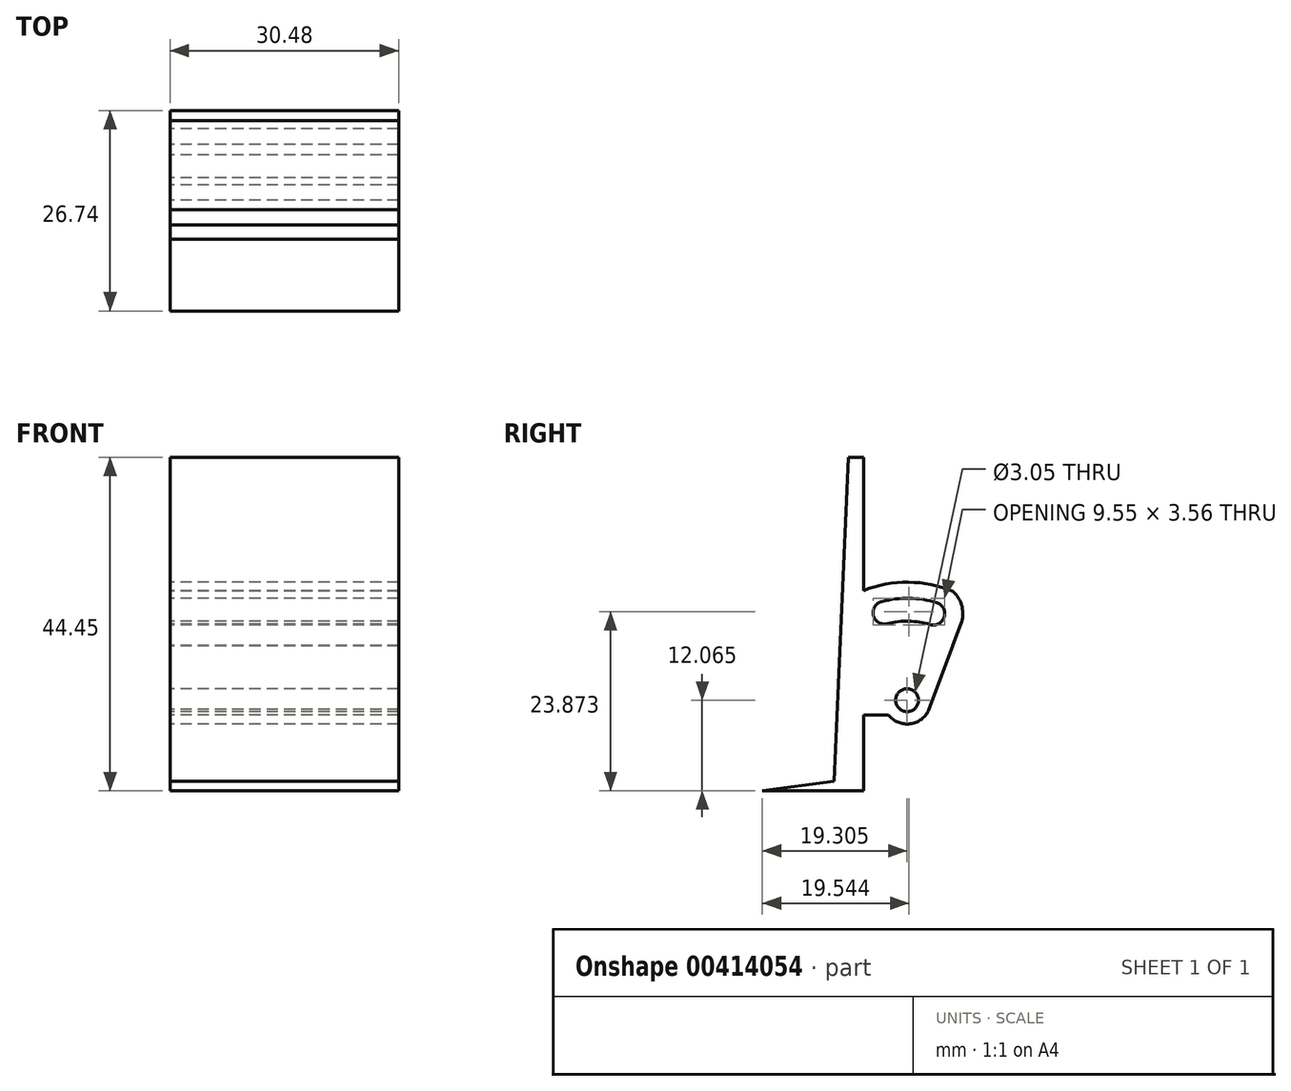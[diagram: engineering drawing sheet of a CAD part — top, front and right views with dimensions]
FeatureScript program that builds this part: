
annotation { "Feature Type Name" : "Feature", "Feature Type Description" : "" }
export const myFeature = defineFeature(function(context is Context, id is Id, definition is map)
    precondition{}
    {
        {
            var Q0;
            Q0=qCreatedBy(makeId("Right.planeOp"),FACE);
            var sketch = newSketch(context, id + "F0", { "sketchPlane" : qUnion([Q0])});
            skLineSegment(sketch, "E0.bottom", {"start": v(0, 0) * mm, "end": v(25.4, 0) * mm});
            skLineSegment(sketch, "E0.top", {"start": v(0, 44.45) * mm, "end": v(25.4, 44.45) * mm});
            skLineSegment(sketch, "E0.left", {"start": v(0, 0) * mm, "end": v(0, 44.45) * mm});
            skLineSegment(sketch, "E0.right", {"start": v(25.4, 0) * mm, "end": v(25.4, 19.37) * mm});
            skLineSegment(sketch, "E1", {"start": v(25.4, 0) * mm, "end": v(25.4, 12.07) * mm});
            skLineSegment(sketch, "E2", {"start": v(25.4, 12.07) * mm, "end": v(25.4, 19.37) * mm});
            skCircle(sketch, "E3", {"center": v(19.3, 12.07) * mm, "radius": 1.52 * mm});
            skArc(sketch, "E4", {"start": v(23.25, 25.07) * mm, "mid": v(19.58, 25.65) * mm, "end": v(15.9, 25.22) * mm});
            skArc(sketch, "E5", {"start": v(22.36, 22.15) * mm, "mid": v(24.26, 23.17) * mm, "end": v(23.25, 25.07) * mm});
            skArc(sketch, "E6", {"start": v(22.36, 22.15) * mm, "mid": v(19.52, 22.6) * mm, "end": v(16.66, 22.27) * mm});
            skPoint(sketch, "E7.center.orphan", {"position": v(19.3, 24.13) * mm});
            skArc(sketch, "E8", {"start": v(16.82, 10.09) * mm, "mid": v(19.86, 8.94) * mm, "end": v(22.32, 11.07) * mm});
            skArc(sketch, "E9", {"start": v(25.4, 26.57) * mm, "mid": v(19.45, 27.8) * mm, "end": v(13.48, 26.68) * mm});
            skLineSegment(sketch, "E10", {"start": v(16.82, 10.09) * mm, "end": v(13.48, 10.09) * mm});
            skArc(sketch, "E11", {"start": v(15.9, 25.22) * mm, "mid": v(14.8, 23.36) * mm, "end": v(16.66, 22.27) * mm});
            skLineSegment(sketch, "E12", {"start": v(13.48, 10.09) * mm, "end": v(13.48, 0) * mm});
            skLineSegment(sketch, "E13", {"start": v(13.48, 26.68) * mm, "end": v(13.48, 44.45) * mm});
            skLineSegment(sketch, "E14", {"start": v(12.7, 44.45) * mm, "end": v(13.48, 44.45) * mm});
            skPoint(sketch, "E15.start.orphan", {"position": v(14.75, 23.74) * mm});
            skLineSegment(sketch, "E16", {"start": v(25.4, 19.37) * mm, "end": v(26.48, 22.21) * mm});
            skArc(sketch, "E17.trimOffspring", {"start": v(26.48, 22.21) * mm, "mid": v(26.62, 24.56) * mm, "end": v(25.4, 26.57) * mm});
            skLineSegment(sketch, "E18.trimOffspring", {"start": v(25.4, 26.57) * mm, "end": v(25.4, 44.45) * mm});
            skLineSegment(sketch, "E19", {"start": v(26.48, 22.21) * mm, "end": v(22.23, 10.84) * mm});
            skLineSegment(sketch, "E20", {"start": v(0, 0) * mm, "end": v(9.58, 1.26) * mm});
            skLineSegment(sketch, "E21", {"start": v(13.48, 44.45) * mm, "end": v(11.45, 44.45) * mm});
            skLineSegment(sketch, "E22", {"start": v(11.45, 44.45) * mm, "end": v(9.58, 1.26) * mm});
            skSolve(sketch);
        }
        {
            var Q0;
            Q0=makeQuery(id+"F0.imprint","IMPRINT",FACE,{"disambiguationData":[TD([[makeQuery(id+"F0.imprint","IMPRINT",EDGE,{"derivedFrom":sQuery(id+"F0.wireOp",EDGE,"E3")}),-1.0]])]});
            extrude(context, id + "F1", {"entities" : qUnion([Q0]), "depth" : 30.48 * mm, "offsetDistance" : 25.4 * mm});
        }
    });
